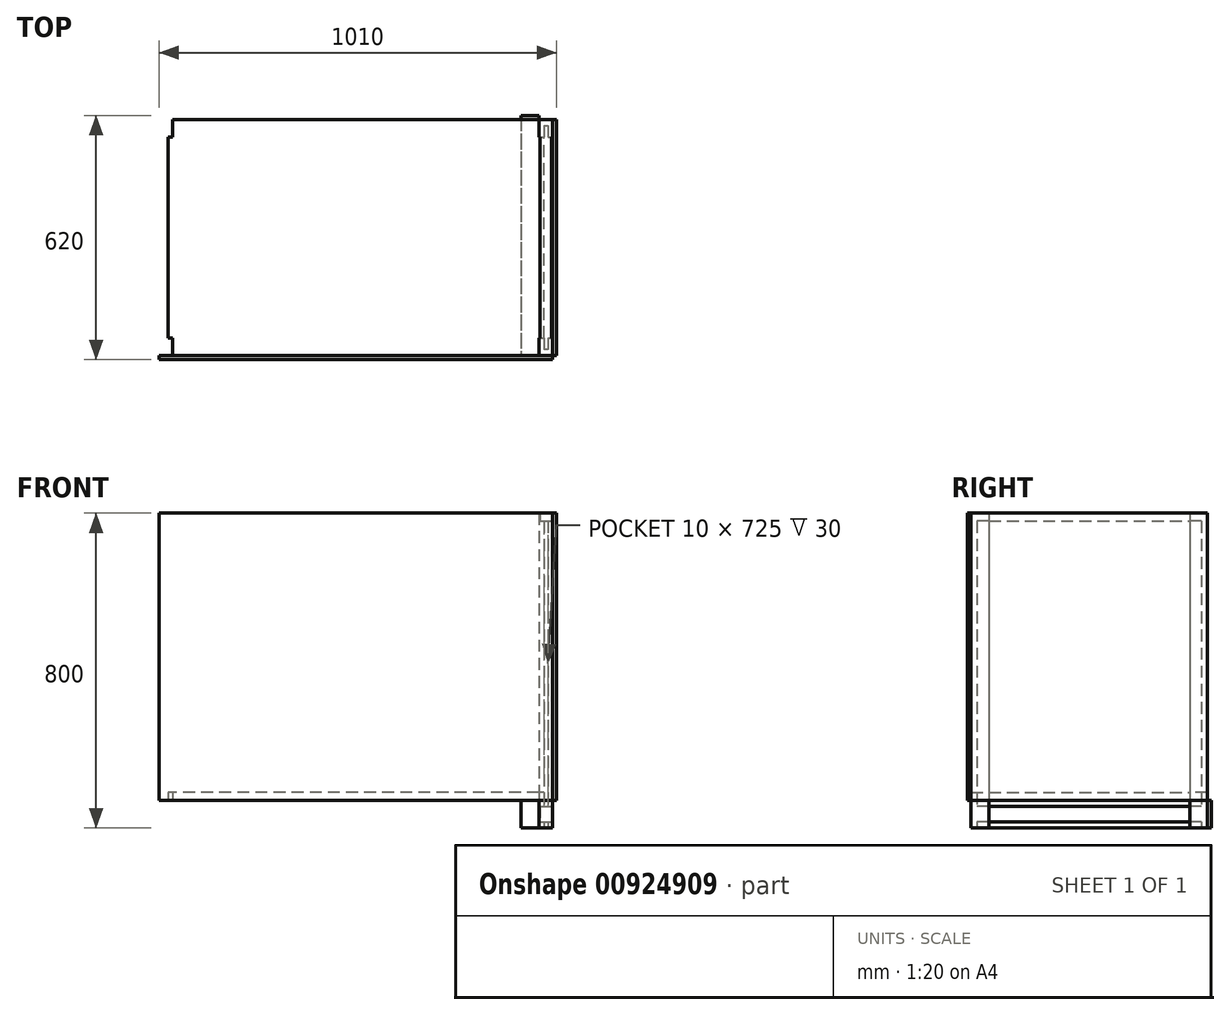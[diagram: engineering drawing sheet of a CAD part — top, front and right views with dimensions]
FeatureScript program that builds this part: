
annotation { "Feature Type Name" : "Feature", "Feature Type Description" : "" }
export const myFeature = defineFeature(function(context is Context, id is Id, definition is map)
    precondition{}
    {
        {
            var Q0;
            Q0=qCreatedBy(makeId("Top.planeOp"),FACE);
            var sketch = newSketch(context, id + "F0", { "sketchPlane" : qUnion([Q0])});
            skLineSegment(sketch, "E0.bottom", {"start": v(-17.5, 300) * mm, "end": v(17.5, 300) * mm});
            skLineSegment(sketch, "E0.top", {"start": v(-17.5, 255) * mm, "end": v(-5, 255) * mm});
            skLineSegment(sketch, "E0.left", {"start": v(-17.5, 300) * mm, "end": v(-17.5, 255) * mm});
            skLineSegment(sketch, "E0.right", {"start": v(17.5, 300) * mm, "end": v(17.5, 255) * mm});
            skLineSegment(sketch, "E1.bottom", {"start": v(-5, 285) * mm, "end": v(5, 285) * mm});
            skLineSegment(sketch, "E1.left", {"start": v(-5, 285) * mm, "end": v(-5, 255) * mm});
            skLineSegment(sketch, "E1.right", {"start": v(5, 285) * mm, "end": v(5, 255) * mm});
            skLineSegment(sketch, "E2.trimOffspring", {"start": v(5, 255) * mm, "end": v(17.5, 255) * mm});
            skLineSegment(sketch, "E3.bottom", {"start": v(-17.5, -255) * mm, "end": v(-5, -255) * mm});
            skLineSegment(sketch, "E3.top", {"start": v(-17.5, -300) * mm, "end": v(17.5, -300) * mm});
            skLineSegment(sketch, "E3.left", {"start": v(-17.5, -255) * mm, "end": v(-17.5, -300) * mm});
            skLineSegment(sketch, "E3.right", {"start": v(17.5, -255) * mm, "end": v(17.5, -300) * mm});
            skLineSegment(sketch, "E4.top", {"start": v(-5, -285) * mm, "end": v(5, -285) * mm});
            skLineSegment(sketch, "E4.left", {"start": v(-5, -255) * mm, "end": v(-5, -285) * mm});
            skLineSegment(sketch, "E4.right", {"start": v(5, -255) * mm, "end": v(5, -285) * mm});
            skLineSegment(sketch, "E5.trimOffspring", {"start": v(5, -255) * mm, "end": v(17.5, -255) * mm});
            skSolve(sketch);
        }
        {
            var Q0;
            Q0 = qSketchRegion(id + "F0", true);
            extrude(context, id + "F1", {"entities" : qUnion([Q0]), "depth" : 800 * mm, "offsetDistance" : 25 * mm});
        }
        {
            var Q0;
            Q0=makeQuery(id+"F1.opExtrude","SWEPT_FACE",FACE,{"disambiguationData":[OSD([sQuery(id+"F0.wireOp",EDGE,"E1.bottom")])]});
            var sketch = newSketch(context, id + "F2", { "sketchPlane" : qUnion([Q0])});
            skLineSegment(sketch, "E6.bottom", {"start": v(-15, 800) * mm, "end": v(15, 800) * mm});
            skLineSegment(sketch, "E6.top", {"start": v(-15, 780) * mm, "end": v(15, 780) * mm});
            skLineSegment(sketch, "E6.left", {"start": v(-15, 800) * mm, "end": v(-15, 780) * mm});
            skLineSegment(sketch, "E6.right", {"start": v(15, 800) * mm, "end": v(15, 780) * mm});
            skLineSegment(sketch, "E7.bottom", {"start": v(-15, 55) * mm, "end": v(15, 55) * mm});
            skLineSegment(sketch, "E7.top", {"start": v(-15, 15) * mm, "end": v(15, 15) * mm});
            skLineSegment(sketch, "E7.left", {"start": v(-15, 55) * mm, "end": v(-15, 15) * mm});
            skLineSegment(sketch, "E7.right", {"start": v(15, 55) * mm, "end": v(15, 15) * mm});
            skSolve(sketch);
        }
        {
            var Q0;
            Q0 = qSketchRegion(id + "F2", true);
            var Q1;
            Q1=makeQuery(id+"F1.opExtrude","SWEPT_FACE",FACE,{"disambiguationData":[OSD([sQuery(id+"F0.wireOp",EDGE,"E4.top")])]});
            extrude(context, id + "F3", {"entities" : qUnion([Q0]), "operationType" : NewBodyOperationType.ADD, "endBound" : BoundingType.UP_TO_SURFACE, "depth" : 25 * mm, "endBoundEntityFace" : qUnion([Q1]), "offsetDistance" : 25 * mm});
        }
        {
            var Q0;
            Q0=makeQuery(id+"F1.opExtrude","SWEPT_FACE",FACE,{"disambiguationData":[OSD([sQuery(id+"F0.wireOp",EDGE,"E3.top")])]});
            var sketch = newSketch(context, id + "F4", { "sketchPlane" : qUnion([Q0])});
            skLineSegment(sketch, "E8.bottom", {"start": v(-62.5, 70) * mm, "end": v(-17.5, 70) * mm});
            skLineSegment(sketch, "E8.top", {"start": v(-62.5, 0) * mm, "end": v(-17.5, 0) * mm});
            skLineSegment(sketch, "E8.left", {"start": v(-62.5, 70) * mm, "end": v(-62.5, 0) * mm});
            skLineSegment(sketch, "E8.right", {"start": v(-17.5, 70) * mm, "end": v(-17.5, 0) * mm});
            skSolve(sketch);
        }
        {
            var Q0;
            Q0 = qSketchRegion(id + "F4", true);
            extrude(context, id + "F5", {"entities" : qUnion([Q0]), "oppositeDirection" : true, "depth" : 610 * mm, "offsetDistance" : 25 * mm});
        }
        {
            var Q0;
            Q0=makeQuery(id+"F1.opExtrude","SWEPT_FACE",FACE,{"disambiguationData":[OSD([sQuery(id+"F0.wireOp",EDGE,"E3.top")])]});
            var sketch = newSketch(context, id + "F6", { "sketchPlane" : qUnion([Q0])});
            skLineSegment(sketch, "E9.bottom", {"start": v(-982.5, 800) * mm, "end": v(17.5, 800) * mm});
            skLineSegment(sketch, "E9.top", {"start": v(-982.5, 70) * mm, "end": v(17.5, 70) * mm});
            skLineSegment(sketch, "E9.left", {"start": v(-982.5, 800) * mm, "end": v(-982.5, 70) * mm});
            skLineSegment(sketch, "E9.right", {"start": v(17.5, 800) * mm, "end": v(17.5, 70) * mm});
            skSolve(sketch);
        }
        {
            var Q0;
            Q0 = qSketchRegion(id + "F6", true);
            extrude(context, id + "F7", {"entities" : qUnion([Q0]), "depth" : 10 * mm, "offsetDistance" : 25 * mm});
        }
        {
            var Q0;
            Q0=makeQuery(id+"F1.opExtrude","SWEPT_FACE",FACE,{"disambiguationData":[OSD([sQuery(id+"F0.wireOp",EDGE,"E3.right")])]});
            var sketch = newSketch(context, id + "F8", { "sketchPlane" : qUnion([Q0])});
            skLineSegment(sketch, "E10.bottom", {"start": v(-300, 800) * mm, "end": v(300, 800) * mm});
            skLineSegment(sketch, "E10.top", {"start": v(-300, 70) * mm, "end": v(300, 70) * mm});
            skLineSegment(sketch, "E10.left", {"start": v(-300, 800) * mm, "end": v(-300, 70) * mm});
            skLineSegment(sketch, "E10.right", {"start": v(300, 800) * mm, "end": v(300, 70) * mm});
            skSolve(sketch);
        }
        {
            var Q0;
            Q0 = qSketchRegion(id + "F8", true);
            extrude(context, id + "F9", {"entities" : qUnion([Q0]), "depth" : 10 * mm, "offsetDistance" : 25 * mm});
        }
        {
            var Q0;
            Q0=makeQuery(id+"F5.opExtrude","SWEPT_FACE",FACE,{"disambiguationData":[OSD([sQuery(id+"F4.wireOp",EDGE,"E8.bottom")])]});
            var sketch = newSketch(context, id + "F10", { "sketchPlane" : qUnion([Q0])});
            skLineSegment(sketch, "E11.bottom", {"start": v(-5, -255) * mm, "end": v(-17.5, -255) * mm});
            skLineSegment(sketch, "E11.top", {"start": v(-5, 255) * mm, "end": v(-17.5, 255) * mm});
            skLineSegment(sketch, "E11.left", {"start": v(-5, -255) * mm, "end": v(-5, 255) * mm});
            skLineSegment(sketch, "E11.right", {"start": v(-960, -255) * mm, "end": v(-960, 255) * mm});
            skLineSegment(sketch, "E12.bottom", {"start": v(-17.5, -300) * mm, "end": v(-947.5, -300) * mm});
            skLineSegment(sketch, "E12.top", {"start": v(-17.5, 300) * mm, "end": v(-947.5, 300) * mm});
            skLineSegment(sketch, "E12.left", {"start": v(-17.5, -300) * mm, "end": v(-17.5, -255) * mm});
            skLineSegment(sketch, "E12.right", {"start": v(-947.5, -300) * mm, "end": v(-947.5, -255) * mm});
            skLineSegment(sketch, "E13", {"start": v(-482.5, 300) * mm, "end": v(-482.5, -300) * mm, "construction": true});
            skLineSegment(sketch, "E14", {"start": v(-5, 0) * mm, "end": v(-960, 0) * mm, "construction": true});
            skLineSegment(sketch, "E15.trimOffspring", {"start": v(-947.5, -255) * mm, "end": v(-960, -255) * mm});
            skLineSegment(sketch, "E16.trimOffspring", {"start": v(-947.5, 255) * mm, "end": v(-947.5, 300) * mm});
            skLineSegment(sketch, "E17.trimOffspring", {"start": v(-947.5, 255) * mm, "end": v(-960, 255) * mm});
            skLineSegment(sketch, "E18.trimOffspring", {"start": v(-17.5, 255) * mm, "end": v(-17.5, 300) * mm});
            skSolve(sketch);
        }
        {
            var Q0;
            Q0 = qSketchRegion(id + "F10", true);
            extrude(context, id + "F11", {"entities" : qUnion([Q0]), "depth" : 20 * mm, "offsetDistance" : 25 * mm});
        }
    });
